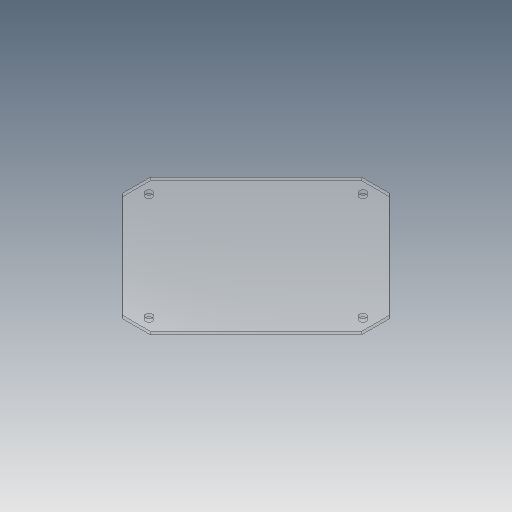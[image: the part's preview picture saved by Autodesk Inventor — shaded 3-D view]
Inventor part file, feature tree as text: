
AUTODESK INVENTOR PART (.ipt)
format: ipt  version: 2017 (Build 210142000, 142)  size: 119,296 bytes
history: native  units: mm
features: sketch x3, extrude x2, hole x1, pattern_circular x1, projected_geometry x1
ambient origin geometry x8: Origin, YZ Plane, XZ Plane, XY Plane, X Axis, Y Axis, Z Axis, Center Point
bodies: Solid1 (feature_tree)
feature tree (8):
  extrude  "Extrusion1"  Depth=40.0mm TaperAngle=360.0deg
  hole  "Hole1"  [1 undecoded]
  pattern_circular  "Circular Pattern1"  Count=15  [1 undecoded]
  extrude  "Extrusion2"  Depth=150.0mm
  sketch  "Sketch1"  dims[d7=2.38125mm d8=0.0mm]
  sketch  "Sketch2"  dims[d11=5.5mm d12=6.0mm d13=5.715mm d14=2.0mm d15=14.3117mm d16=8.0mm d17=20.594885mm d18=40.0mm d19=360.0deg]
  sketch  "Sketch3"  dims[d25=190.0mm d26=10.0mm d27=150.0mm d28=150.0mm d29=10.0mm d30=0.0mm]
  projected_geometry  "Projected Loop1"
note: 2 required parameter values undecoded (feature->parameter linkage not recoverable at this tier; creation-order binding heuristic only, values carry confidence <= 0.55)
